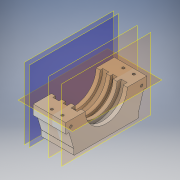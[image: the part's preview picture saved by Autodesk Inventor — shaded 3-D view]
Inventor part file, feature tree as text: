
AUTODESK INVENTOR PART (.ipt)
format: ipt  version: 2019 (Build 230136000, 136)  size: 532,992 bytes
history: native  units: mm
features: sketch x26, extrude x21, mirror x13, plane x12, projected_geometry x11, other x4, fillet x4, hole x3
ambient origin geometry x8: Origin, YZ Plane, XZ Plane, XY Plane, X Axis, Y Axis, Z Axis, Center Point
bodies: Body1 (feature_tree)
feature tree (94):
  other  "實體1"
  extrude  "擠出1"  Depth=123.43mm
  plane  "工作平面2"
  extrude  "擠出3"  Depth=160.0mm
  plane  "工作平面3"
  extrude  "擠出4"  Depth=120.0mm TaperAngle=0.0deg
  extrude  "擠出5"  [1 undecoded]
  plane  "工作平面4"
  extrude  "擠出7"  Depth=130.0mm
  plane  "工作平面5"
  extrude  "擠出9"  Depth=15.0mm TaperAngle=0.0deg
  extrude  "擠出10"  [1 undecoded]
  extrude  "擠出11"  Depth=111.375mm
  extrude  "擠出12"  Depth=10.0mm TaperAngle=0.0deg
  mirror  "鏡射1"
  fillet  "圓角2"  Radius=10.0mm
  fillet  "圓角3"  Radius=10.0mm
  sketch  "草圖16"
  plane  "工作平面7"
  mirror  "鏡射2"
  fillet  "圓角5"  [1 undecoded]
  fillet  "圓角6"  Radius=10.0mm
  plane  "工作平面8"
  plane  "工作平面9"
  sketch  "草圖20"
  extrude  "擠出15"  [1 undecoded]
  plane  "工作平面10"
  extrude  "擠出16"  Depth=10.0mm
  extrude  "擠出17"  Depth=10.0mm TaperAngle=0.0deg
  plane  "工作平面11"
  extrude  "擠出19"  Depth=10.0mm TaperAngle=0.0deg
  extrude  "擠出20"  Depth=160.0mm
  mirror  "鏡射3"
  mirror  "鏡射4"
  extrude  "擠出21"  Depth=80.0mm
  mirror  "鏡射7"
  plane  "工作平面15"
  mirror  "鏡射9"
  hole  "孔2"  [1 undecoded]
  mirror  "鏡射10"
  mirror  "鏡射11"
  hole  "孔3"  [1 undecoded]
  mirror  "鏡射12"
  mirror  "鏡射13"
  extrude  "擠出22"  Depth=160.0mm
  extrude  "擠出23"  Depth=120.0mm TaperAngle=0.0deg
  extrude  "擠出24"  Depth=120.0mm TaperAngle=0.0deg
  extrude  "擠出25"  Depth=25.0mm
  extrude  "擠出27"  Depth=20.0mm
  extrude  "擠出28"  Depth=2.0mm
  mirror  "鏡射14"
  plane  "工作平面17"
  hole  "孔4"  [1 undecoded]
  mirror  "鏡射15"
  mirror  "鏡射16"
  other  "分割2"
  other  "分割3"
  other  "分割4"
  sketch  "草圖1"
  sketch  "草圖4"
  sketch  "草圖6"
  sketch  "草圖7"
  projected_geometry  "投影迴路1"
  sketch  "草圖9"
  projected_geometry  "投影迴路4"
  sketch  "草圖11"
  sketch  "草圖12"
  projected_geometry  "投影迴路6"
  sketch  "草圖13"
  projected_geometry  "投影迴路7"
  sketch  "草圖14"
  plane  "工作平面6"
  sketch  "草圖17"
  projected_geometry  "投影迴路8"
  sketch  "草圖24"
  projected_geometry  "投影迴路11"
  sketch  "草圖25"
  sketch  "草圖26"
  sketch  "草圖27"
  sketch  "草圖28"
  sketch  "草圖29"
  projected_geometry  "投影迴路12"
  sketch  "草圖30"
  sketch  "草圖31"
  sketch  "草圖32"
  projected_geometry  "投影迴路13"
  projected_geometry  "投影迴路14"
  projected_geometry  "投影迴路15"
  sketch  "草圖33"
  sketch  "草圖34"
  sketch  "草圖35"
  projected_geometry  "投影迴路16"
  sketch  "草圖36"
  sketch  "草圖37"
note: 7 required parameter values undecoded (feature->parameter linkage not recoverable at this tier; creation-order binding heuristic only, values carry confidence <= 0.55)
